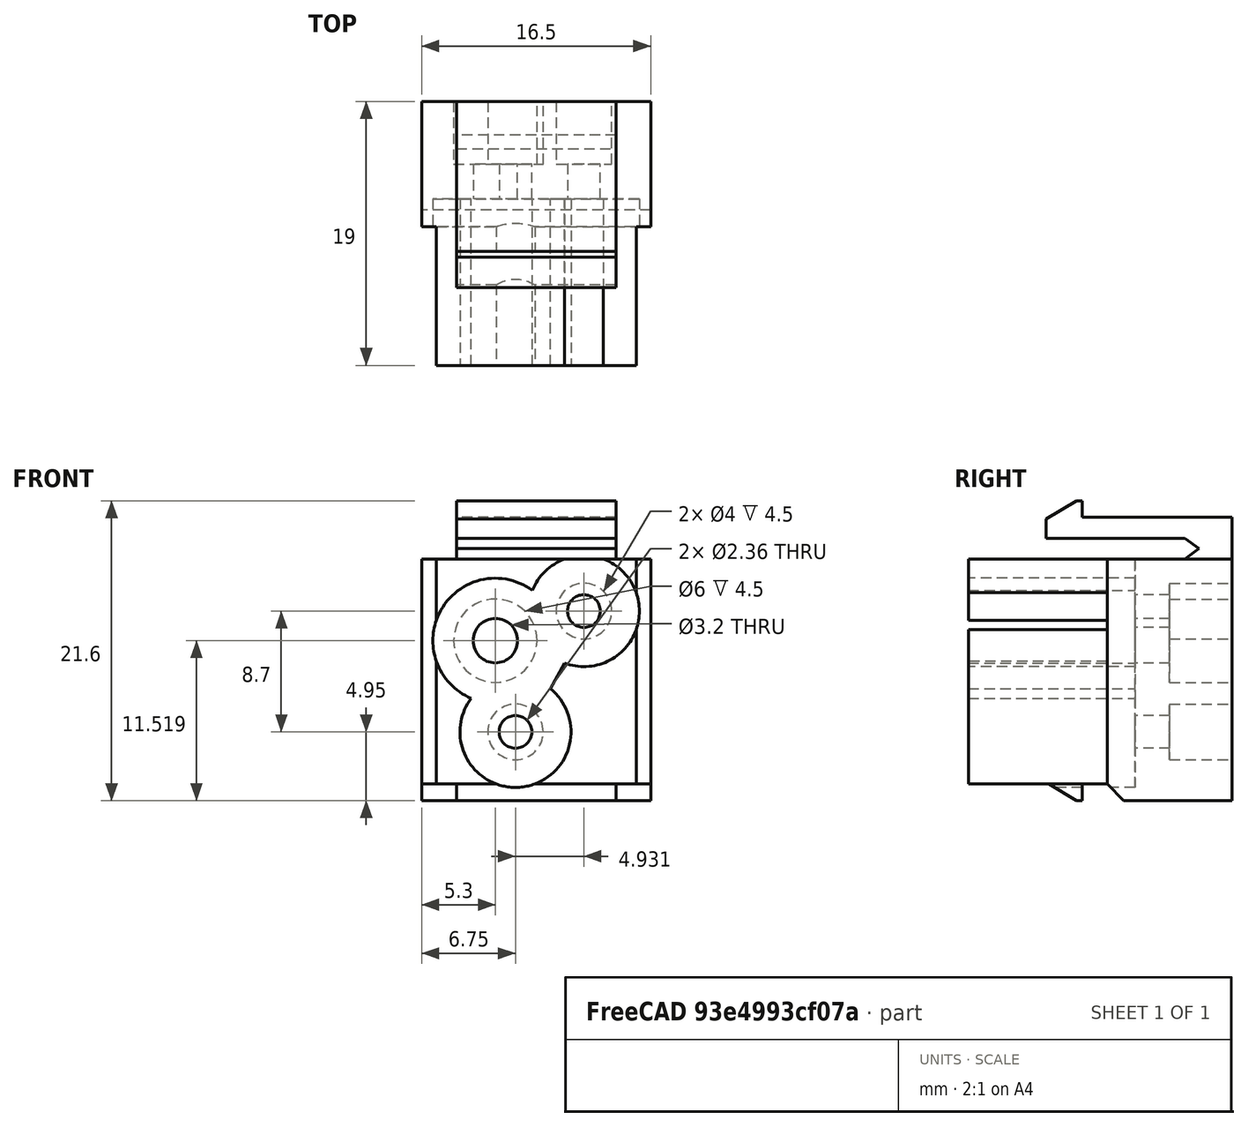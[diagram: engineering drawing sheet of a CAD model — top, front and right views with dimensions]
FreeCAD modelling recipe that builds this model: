
FCSTD DOCUMENT  (FreeCAD 1.0R39319 (Git))
Label: IEC_C6_Keystone
License: All rights reserved
LicenseURL: https://en.wikipedia.org/wiki/All_rights_reserved
objects: Sketcher::SketchObject×4, PartDesign::Pad×3, PartDesign::Pocket×3, Part::Feature×1, PartDesign::FeatureBase×1, PartDesign::Chamfer×1, PartDesign::Body×1, App::Part×1, App::FeaturePython×1, Assembly::JointGroup×1, Assembly::AssemblyObject×1
note: 33 computed .brp shape members not serialized (recipe doc carries the construction recipe); baked Part::Feature solids carry a one-line shape summary decoded from their .brp

FEATURE [Part::Feature] keystone_blank_insert_chamfer002_solid  label="keystone_blank_insert_chamfer002 (Solid)"
  shape: bbox 16.5 x 19 x 21.6 mm, 39 faces (baked)
FEATURE [PartDesign::FeatureBase] BaseFeature
  BaseFeature = -> keystone_blank_insert_chamfer002_solid
  Suppressed = false
FEATURE [PartDesign::Pad] Pad003
  BaseFeature = -> BaseFeature
  Direction = (0,6e-16,-1)
  Length = 10
  Length2 = 10
  Profile = -> BaseFeature [Face1]
  Refine = true
  Suppressed = false
  Type = 3
  UpToFace = -> BaseFeature [Face8]
FEATURE [PartDesign::Pad] Pad
  BaseFeature = -> Pad003
  Direction = (0,-1,0)
  Length = 10
  Length2 = 10
  Profile = -> BaseFeature [Face3]
  Refine = true
  Suppressed = false
  Type = 3
  UpToFace = -> BaseFeature [Face25]
FEATURE [Sketcher::SketchObject] Sketch
  ArcFitTolerance = 1e-06
  AttachmentSupport = -> [Pad]
  FullyConstrained = true
  MakeInternals = false
  MapMode = 5
  Placement = pos=(0,19,0) rot=(0,0.707107,0.707107;3.14159rad)
  sketch-geometry (4):
    g0: LineSegment StartX=-15.45 StartY=1.42e-14 StartZ=0 EndX=-15.45 EndY=-1.2 EndZ=0
    g1: LineSegment StartX=-15.45 StartY=-1.2 StartZ=0 EndX=1.05 EndY=-1.2 EndZ=0
    g2: LineSegment StartX=1.05 StartY=-1.2 StartZ=0 EndX=1.05 EndY=1.42e-14 EndZ=0
    g3: LineSegment StartX=1.05 StartY=1.42e-14 StartZ=0 EndX=-15.45 EndY=1.42e-14 EndZ=0
  constraints (11):
    c: Coincident(g0,g1)
    c: Coincident(g1,g2)
    c: Coincident(g2,g3)
    c: Coincident(g3,g0)
    c: Vertical(g0)
    c: Vertical(g2)
    c: Horizontal(g1)
    c: Horizontal(g3)
    c: Distance(g1,g3) = 1.2
    c: Coincident(g0,g-3)
    c: PointOnObject(g-3,g2)
FEATURE [PartDesign::Pad] Pad002
  BaseFeature = -> Pad
  Direction = (0,1,-2e-16)
  Length = 10
  Length2 = 10
  Profile = -> Sketch
  ReferenceAxis = -> Sketch [N_Axis]
  Refine = true
  Reversed = true
  Suppressed = false
  Type = 3
  UpToFace = -> Pad [Face13]
FEATURE [PartDesign::Chamfer] Chamfer
  Angle = 45
  Base = -> Pad002 [Edge66]
  BaseFeature = -> Pad002
  ChamferType = 0
  FlipDirection = false
  Refine = true
  Size = 1.19
  Size2 = 1
  SupportTransform = false
  Suppressed = false
  UseAllEdges = false
FEATURE [Sketcher::SketchObject] Sketch001
  ArcFitTolerance = 1e-06
  AttachmentSupport = -> [Chamfer]
  FullyConstrained = true
  MakeInternals = false
  MapMode = 5
  Placement = pos=(0,0,0) rot=(1,0,0;1.5708rad)
  sketch-geometry (25):
    g0: LineSegment [constr] StartX=-4.10246 StartY=4.70746 StartZ=0 EndX=7.20754 EndY=-1.70221 EndZ=0
    g1: LineSegment [constr] StartX=7.20754 StartY=-1.70221 StartZ=0 EndX=16.0825 EndY=13.9578 EndZ=0
    g2: LineSegment [constr] StartX=16.0825 StartY=13.9578 StartZ=0 EndX=4.77246 EndY=20.3675 EndZ=0
    g3: LineSegment [constr] StartX=4.77246 StartY=20.3675 StartZ=0 EndX=-4.10246 EndY=4.70746 EndZ=0
    g4: LineSegment [constr] StartX=1.77004 StartY=1.37937 StartZ=0 EndX=10.645 EndY=17.0394 EndZ=0
    g5: LineSegment [constr] StartX=0.335 StartY=12.5375 StartZ=0 EndX=11.645 EndY=6.12779 EndZ=0
    g6: GeomPoint [constr] X=5.69974 Y=3.75 Z=0
    g7: GeomPoint [constr] X=10.6303 Y=12.45 Z=0
    g8: GeomPoint [constr] X=4.25 Y=10.3187 Z=0
    g9: LineSegment [constr] StartX=5.69974 StartY=3.75 StartZ=0 EndX=10.6303 EndY=12.45 EndZ=0
    g10: GeomPoint [constr] X=8.165 Y=8.1 Z=0
    g11: Circle [constr] CenterX=4.25 CenterY=10.3187 CenterZ=0 NormalX=0 NormalY=0 NormalZ=1 AngleXU=0 Radius=1.6
    g12: Circle [constr] CenterX=5.69974 CenterY=3.75 CenterZ=0 NormalX=0 NormalY=0 NormalZ=1 AngleXU=0 Radius=1.18
    g13: Circle [constr] CenterX=10.6303 CenterY=12.45 CenterZ=0 NormalX=0 NormalY=0 NormalZ=1 AngleXU=0 Radius=1.18
    g14: ArcOfCircle CenterX=5.69974 CenterY=3.75 CenterZ=0 NormalX=0 NormalY=0 NormalZ=1 AngleXU=0 Radius=4 StartAngle=2.49261 EndAngle=7.17516
    g15: ArcOfCircle CenterX=4.25 CenterY=10.3187 CenterZ=0 NormalX=0 NormalY=0 NormalZ=1 AngleXU=0 Radius=4.5 StartAngle=0.935912 EndAngle=4.31609
    g16: ArcOfCircle CenterX=10.6303 CenterY=12.45 CenterZ=0 NormalX=0 NormalY=0 NormalZ=1 AngleXU=0 Radius=4 StartAngle=4.36002 EndAngle=9.04257
    g17: LineSegment StartX=8.21124 StartY=6.86326 StartZ=0 EndX=9.24977 EndY=8.69577 EndZ=0
    g18: LineSegment [constr] StartX=0 StartY=0 StartZ=0 EndX=14.4 EndY=0 EndZ=0
    g19: LineSegment [constr] StartX=14.4 StartY=0 StartZ=0 EndX=14.4 EndY=16.2 EndZ=0
    g20: LineSegment [constr] StartX=14.4 StartY=16.2 StartZ=0 EndX=0 EndY=16.2 EndZ=0
    g21: LineSegment [constr] StartX=0 StartY=16.2 StartZ=0 EndX=0 EndY=0 EndZ=0
    g22: Circle [constr] CenterX=4.25 CenterY=10.3187 CenterZ=0 NormalX=0 NormalY=0 NormalZ=1 AngleXU=0 Radius=4.25
    g23: Circle [constr] CenterX=10.6303 CenterY=12.45 CenterZ=0 NormalX=0 NormalY=0 NormalZ=1 AngleXU=0 Radius=3.75
    g24: Circle [constr] CenterX=5.69974 CenterY=3.75 CenterZ=0 NormalX=0 NormalY=0 NormalZ=1 AngleXU=0 Radius=3.75
  constraints (61):
    c: Coincident(g0,g1)
    c: Coincident(g1,g2)
    c: Coincident(g2,g3)
    c: Coincident(g3,g0)
    c: Perpendicular(g3,g0)
    c: Perpendicular(g3,g2)
    c: Perpendicular(g0,g1)
    c: Distance(g3,g3) = 18
    c: Distance(g0,g0) = 13
    c: Symmetric(g3,g3,g5)
    c: Symmetric(g1,g1,g5)
    c: PointOnObject(g8,g5)
    c: Distance(g8,g4) = 2.25
    c: Distance(g6,g4) = 2.25
    c: Distance(g7,g4) = 2.25
    c: Coincident(g9,g6)
    c: Coincident(g9,g7)
    c: Symmetric(g9,g9,g10)
    c: PointOnObject(g10,g5)
    c: Distance(g9,g9) = 10
    c: Diameter(g11) = 3.2
    c: Coincident(g11,g8)
    c: Diameter(g12) = 2.36
    c: Coincident(g12,g6)
    c: Coincident(g13,g7)
    c: Equal(g13,g12)
    c: Coincident(g14,g6)
    c: Tangent(g14,g0)
    c: Coincident(g15,g8)
    c: Coincident(g15,g14)
    c: Tangent(g15,g3)
    c: Perpendicular(g2,g4)
    c: PointOnObject(g4,g0)
    c: PointOnObject(g4,g2)
    c: Tangent(g1,g14)
    c: Coincident(g16,g7)
    c: Coincident(g16,g15)
    c: Tangent(g16,g2)
    c: Coincident(g17,g14)
    c: Coincident(g17,g16)
    c: Perpendicular(g5,g17)
    c: Distance(g7,g17) = 0.65
    c: Coincident(g18,g19)
    c: Coincident(g19,g20)
    c: Coincident(g20,g21)
    c: Coincident(g21,g18)
    c: Horizontal(g18)
    c: Horizontal(g20)
    c: Vertical(g19)
    c: Vertical(g21)
    c: Coincident(g18,g-1)
    c: Coincident(g19,g-3)
    c: Diameter(g22) = 8.5
    c: Coincident(g22,g8)
    c: Coincident(g23,g7)
    c: Coincident(g24,g6)
    c: Equal(g24,g23)
    c: Diameter(g23) = 7.5
    c: Tangent(g22,g21)
    c: Tangent(g23,g20)
    c: Tangent(g24,g18)
FEATURE [PartDesign::Pocket] Pocket
  BaseFeature = -> Chamfer
  Direction = (0,1,-2e-16)
  Length = 12
  Length2 = 5
  Profile = -> Sketch001
  ReferenceAxis = -> Sketch001 [N_Axis]
  Refine = true
  Suppressed = false
  Type = 0
FEATURE [Sketcher::SketchObject] Sketch002
  ArcFitTolerance = 1e-06
  AttachmentSupport = -> [Pocket]
  ExternalGeometry = -> [Pocket]
  FullyConstrained = true
  MakeInternals = false
  MapMode = 5
  Placement = pos=(0,12,0) rot=(1,0,0;1.5708rad)
  sketch-geometry (3):
    g0: Circle CenterX=4.25 CenterY=10.3187 CenterZ=0 NormalX=0 NormalY=0 NormalZ=1 AngleXU=0 Radius=1.6
    g1: Circle CenterX=10.6303 CenterY=12.45 CenterZ=0 NormalX=0 NormalY=0 NormalZ=1 AngleXU=0 Radius=1.18
    g2: Circle CenterX=5.69974 CenterY=3.75 CenterZ=0 NormalX=0 NormalY=0 NormalZ=1 AngleXU=0 Radius=1.18
  constraints (6):
    c: Diameter(g0) = 3.2
    c: Coincident(g0,g-3)
    c: Diameter(g1) = 2.36
    c: Coincident(g1,g-5)
    c: Coincident(g2,g-4)
    c: Equal(g2,g1)
FEATURE [PartDesign::Pocket] Pocket001
  BaseFeature = -> Pocket
  Direction = (0,1,-2e-16)
  Length = 5
  Length2 = 5
  Profile = -> Sketch002
  ReferenceAxis = -> Sketch002 [N_Axis]
  Refine = true
  Suppressed = false
  Type = 1
FEATURE [Sketcher::SketchObject] Sketch003
  ArcFitTolerance = 1e-06
  AttachmentSupport = -> [Pocket001]
  ExternalGeometry = -> [Pocket001]
  FullyConstrained = true
  MakeInternals = false
  MapMode = 5
  Placement = pos=(0,19,0) rot=(0,0.707107,0.707107;3.14159rad)
  sketch-geometry (3):
    g0: Circle CenterX=-10.6303 CenterY=12.45 CenterZ=0 NormalX=0 NormalY=0 NormalZ=1 AngleXU=0 Radius=2
    g1: Circle CenterX=-5.69974 CenterY=3.75 CenterZ=0 NormalX=0 NormalY=0 NormalZ=1 AngleXU=0 Radius=2
    g2: Circle CenterX=-4.25 CenterY=10.3187 CenterZ=0 NormalX=0 NormalY=0 NormalZ=1 AngleXU=0 Radius=3
  constraints (6):
    c: Diameter(g0) = 4
    c: Coincident(g0,g-3)
    c: Coincident(g1,g-5)
    c: Equal(g1,g0)
    c: Diameter(g2) = 6
    c: Coincident(g2,g-4)
FEATURE [PartDesign::Pocket] Pocket002
  BaseFeature = -> Pocket001
  Direction = (0,-1,2e-16)
  Length = 0
  Length2 = 5
  Offset = -2.5
  Profile = -> Sketch003
  ReferenceAxis = -> Sketch003 [N_Axis]
  Refine = true
  Suppressed = false
  Type = 3
  UpToFace = -> Pocket001 [Face23]
FEATURE [PartDesign::Body] Body
  AllowCompound = false
  BaseFeature = -> keystone_blank_insert_chamfer002_solid
  Group = -> [BaseFeature,Pad003,Pad,Sketch,Pad002,Chamfer,Sketch001,Pocket,Sketch002,Pocket001,Sketch003,Pocket002]
  Origin = -> Origin
  Tip = -> Pocket002
FEATURE [App::Part] Part  label="Keystone"
  Group = -> [keystone_blank_insert_chamfer002_solid,Body]
  Origin = -> Origin001
FEATURE [App::FeaturePython] GroundedJoint  # Assembly grounded joint (typed FeaturePython)
  ObjectToGround = -> Part
FEATURE [Assembly::JointGroup] Joints
  Group = -> [GroundedJoint]
FEATURE [Assembly::AssemblyObject] Assembly  label="IEC C6 Keystone"
  Group = -> [Joints,Part,GroundedJoint]
  Origin = -> Origin004
  Type = Assembly
